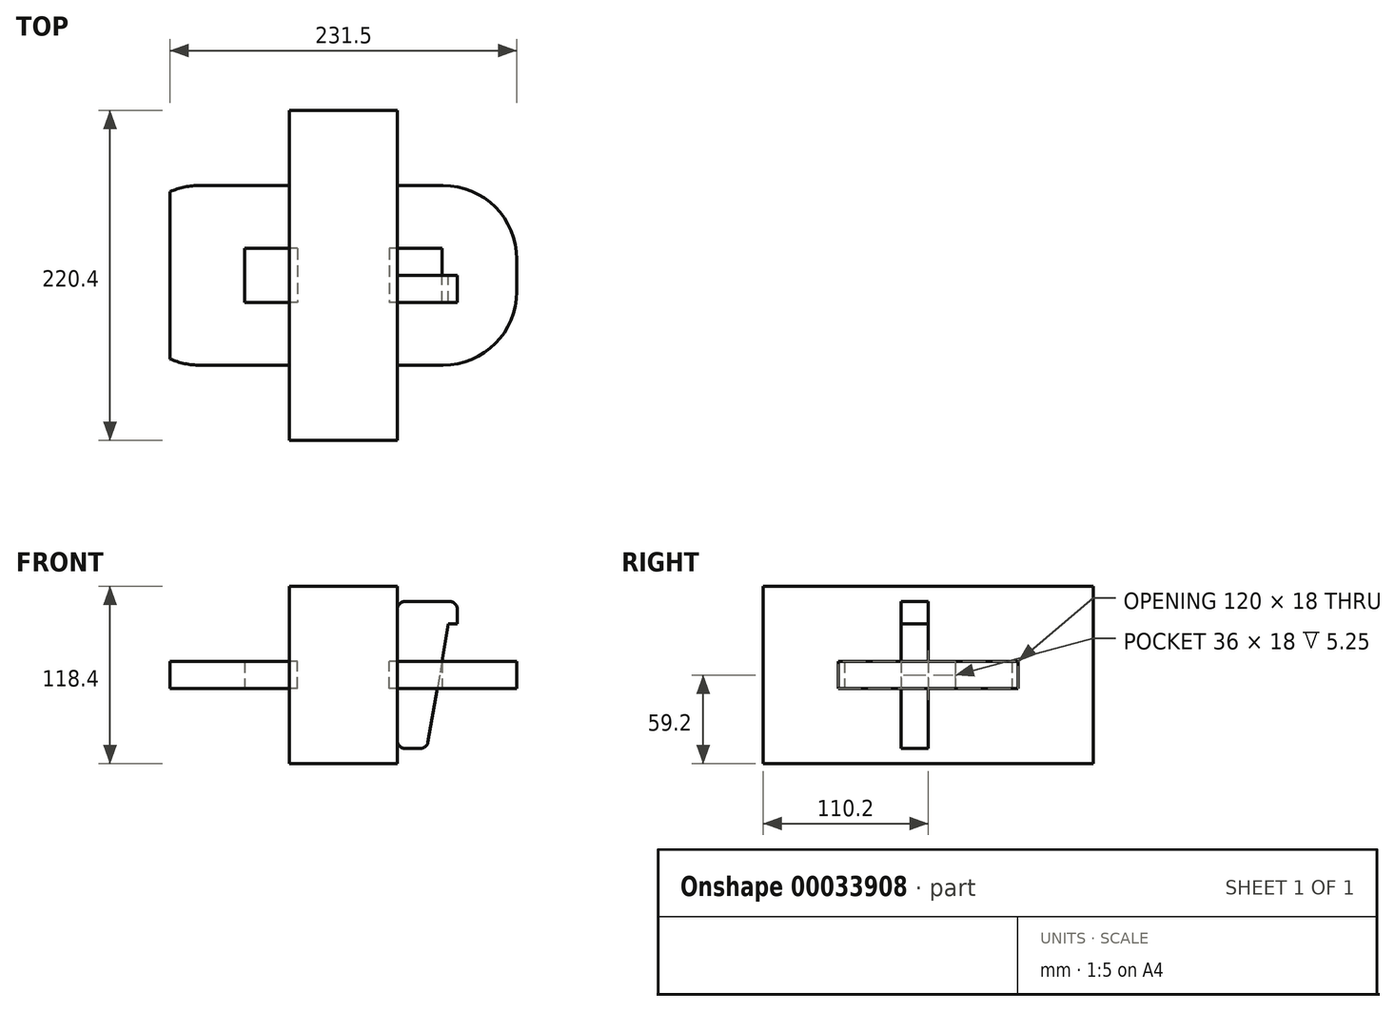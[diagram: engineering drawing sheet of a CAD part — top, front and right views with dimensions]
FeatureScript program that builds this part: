
annotation { "Feature Type Name" : "Feature", "Feature Type Description" : "" }
export const myFeature = defineFeature(function(context is Context, id is Id, definition is map)
    precondition{}
    {
        {
            var Q0;
            Q0=qCreatedBy(makeId("Top.planeOp"),FACE);
            var sketch = newSketch(context, id + "F0", { "sketchPlane" : qUnion([Q0])});
            skLineSegment(sketch, "E0.rect.bottom", {"start": v(95.75, -60) * mm, "end": v(-95.75, -60) * mm});
            skLineSegment(sketch, "E0.rect.top", {"start": v(95.75, 60) * mm, "end": v(-95.75, 60) * mm});
            skLineSegment(sketch, "E0.rect.left", {"start": v(145.75, -10) * mm, "end": v(145.75, 10) * mm});
            skLineSegment(sketch, "E0.rect.right", {"start": v(-145.75, -10) * mm, "end": v(-145.75, 10) * mm});
            skPoint(sketch, "E0.rect.middle", {"position": v(0, 0) * mm});
            skLineSegment(sketch, "E1.rect.bottom", {"start": v(65.75, -18) * mm, "end": v(-65.75, -18) * mm});
            skLineSegment(sketch, "E1.rect.top", {"start": v(65.75, 18) * mm, "end": v(-65.75, 18) * mm});
            skLineSegment(sketch, "E1.rect.left", {"start": v(65.75, -18) * mm, "end": v(65.75, 18) * mm});
            skLineSegment(sketch, "E1.rect.right", {"start": v(-65.75, -18) * mm, "end": v(-65.75, 18) * mm});
            skLineSegment(sketch, "E2", {"start": v(0, 0) * mm, "end": v(0, 60) * mm, "construction": true});
            skLineSegment(sketch, "E3", {"start": v(0, 0) * mm, "end": v(-24.77, 0) * mm, "construction": true});
            skPoint(sketch, "E4.visualSharp", {"position": v(-145.75, 60) * mm});
            skArc(sketch, "E4.filletArc", {"start": v(-95.75, 60) * mm, "mid": v(-131.1, 45.36) * mm, "end": v(-145.75, 10) * mm});
            skPoint(sketch, "E5.visualSharp", {"position": v(-145.75, -60) * mm});
            skArc(sketch, "E5.filletArc", {"start": v(-145.75, -10) * mm, "mid": v(-131.1, -45.36) * mm, "end": v(-95.75, -60) * mm});
            skPoint(sketch, "E6.visualSharp", {"position": v(145.75, 60) * mm});
            skArc(sketch, "E6.filletArc", {"start": v(145.75, 10) * mm, "mid": v(131.1, 45.36) * mm, "end": v(95.75, 60) * mm});
            skPoint(sketch, "E7.visualSharp", {"position": v(145.75, -60) * mm});
            skArc(sketch, "E7.filletArc", {"start": v(95.75, -60) * mm, "mid": v(131.1, -45.36) * mm, "end": v(145.75, -10) * mm});
            skSolve(sketch);
        }
        {
            var Q0;
            Q0 = qSketchRegion(id + "F0", true);
            var Q1;
            Q1=makeQuery(id+"F0.imprint","IMPRINT",FACE,{"disambiguationData":[TD([[makeQuery(id+"F0.imprint","IMPRINT",EDGE,{"derivedFrom":sQuery(id+"F0.wireOp",EDGE,"E0.rect.bottom")}),-1.0]])]});
            extrude(context, id + "F1", {"entities" : qUnion([Q0, Q1]), "depth" : 18 * mm});
        }
        {
            var Q0;
            Q0=qCreatedBy(makeId("Right.planeOp"),FACE);
            var sketch = newSketch(context, id + "F2", { "sketchPlane" : qUnion([Q0])});
            skLineSegment(sketch, "E8.0", {"start": v(-60, 18) * mm, "end": v(-60, 0) * mm});
            skLineSegment(sketch, "E8.1", {"start": v(-60, 18) * mm, "end": v(-10, 18) * mm});
            skLineSegment(sketch, "E8.2", {"start": v(-60, 0) * mm, "end": v(-10, 0) * mm});
            skLineSegment(sketch, "E8.3", {"start": v(-10, 18) * mm, "end": v(10, 18) * mm});
            skLineSegment(sketch, "E8.4", {"start": v(10, 18) * mm, "end": v(60, 18) * mm});
            skLineSegment(sketch, "E8.5", {"start": v(10, 0) * mm, "end": v(60, 0) * mm});
            skLineSegment(sketch, "E8.6", {"start": v(-10, 0) * mm, "end": v(10, 0) * mm});
            skLineSegment(sketch, "E8.7", {"start": v(60, 18) * mm, "end": v(60, 0) * mm});
            skLineSegment(sketch, "E9.0", {"start": v(10, 68.2) * mm, "end": v(110.2, 68.2) * mm});
            skLineSegment(sketch, "E9.1", {"start": v(-10, 68.2) * mm, "end": v(10, 68.2) * mm});
            skLineSegment(sketch, "E9.2", {"start": v(-110.2, 68.2) * mm, "end": v(-10, 68.2) * mm});
            skLineSegment(sketch, "E9.3", {"start": v(-110.2, 68.2) * mm, "end": v(-110.2, -50.2) * mm});
            skLineSegment(sketch, "E9.4", {"start": v(-110.2, -50.2) * mm, "end": v(-10, -50.2) * mm});
            skLineSegment(sketch, "E9.5", {"start": v(110.2, 68.2) * mm, "end": v(110.2, -50.2) * mm});
            skLineSegment(sketch, "E9.6", {"start": v(-10, -50.2) * mm, "end": v(10, -50.2) * mm});
            skLineSegment(sketch, "E9.7", {"start": v(10, -50.2) * mm, "end": v(110.2, -50.2) * mm});
            skSolve(sketch);
        }
        {
            var Q0;
            Q0=makeQuery(id+"F2.imprint","IMPRINT",FACE,{"disambiguationData":[TD([[makeQuery(id+"F2.imprint","IMPRINT",EDGE,{"derivedFrom":sQuery(id+"F2.wireOp",EDGE,"E8.0")}),-1.0]])]});
            extrude(context, id + "F3", {"entities" : qUnion([Q0]), "endBound" : BoundingType.SYMMETRIC, "depth" : 72 * mm});
        }
        {
            var Q0;
            Q0=makeQuery(id+"F1.opExtrude","CAP_FACE",FACE,{"disambiguationData":[OSD([sQuery(id+"F0.wireOp",EDGE,"E0.rect.bottom"),sQuery(id+"F0.wireOp",EDGE,"E0.rect.top"),sQuery(id+"F0.wireOp",EDGE,"E0.rect.left"),sQuery(id+"F0.wireOp",EDGE,"E0.rect.right"),sQuery(id+"F0.wireOp",EDGE,"E1.rect.bottom"),sQuery(id+"F0.wireOp",EDGE,"E1.rect.top"),sQuery(id+"F0.wireOp",EDGE,"E1.rect.left"),sQuery(id+"F0.wireOp",EDGE,"E1.rect.right"),sQuery(id+"F0.wireOp",EDGE,"E4.filletArc"),sQuery(id+"F0.wireOp",EDGE,"E5.filletArc"),sQuery(id+"F0.wireOp",EDGE,"E6.filletArc"),sQuery(id+"F0.wireOp",EDGE,"E7.filletArc")])],"isStart":false});
            var sketch = newSketch(context, id + "F4", { "sketchPlane" : qUnion([Q0])});
            skLineSegment(sketch, "E10", {"start": v(-65.75, -18) * mm, "end": v(-30.75, -18) * mm});
            skLineSegment(sketch, "E11", {"start": v(-30.75, -18) * mm, "end": v(-30.75, 18) * mm});
            skLineSegment(sketch, "E12", {"start": v(-30.75, 18) * mm, "end": v(0, 18) * mm});
            skLineSegment(sketch, "E13", {"start": v(0, 18) * mm, "end": v(0, -18) * mm});
            skLineSegment(sketch, "E14", {"start": v(0, -18) * mm, "end": v(-30.75, -18) * mm});
            skLineSegment(sketch, "E15.MirrorCS", {"start": v(0, -18) * mm, "end": v(30.75, -18) * mm});
            skLineSegment(sketch, "E16.MirrorCS", {"start": v(30.75, -18) * mm, "end": v(30.75, 18) * mm});
            skLineSegment(sketch, "E17.MirrorCS", {"start": v(30.75, 18) * mm, "end": v(0, 18) * mm});
            skSolve(sketch);
        }
        {
            var Q0;
            Q0 = qSketchRegion(id + "F4", true);
            extrude(context, id + "F5", {"entities" : qUnion([Q0]), "operationType" : NewBodyOperationType.ADD, "endBound" : BoundingType.UP_TO_NEXT, "oppositeDirection" : true, "depth" : 25 * mm});
        }
        {
            var Q0;
            Q0=makeQuery(id+"F5.boolean.opBoolean","MERGE",FACE,{"derivedFrom":[makeQuery(id+"F1.opExtrude","CAP_FACE",FACE,{"disambiguationData":[OSD([sQuery(id+"F0.wireOp",EDGE,"E0.rect.bottom"),sQuery(id+"F0.wireOp",EDGE,"E0.rect.top"),sQuery(id+"F0.wireOp",EDGE,"E0.rect.left"),sQuery(id+"F0.wireOp",EDGE,"E0.rect.right"),sQuery(id+"F0.wireOp",EDGE,"E1.rect.bottom"),sQuery(id+"F0.wireOp",EDGE,"E1.rect.top"),sQuery(id+"F0.wireOp",EDGE,"E1.rect.left"),sQuery(id+"F0.wireOp",EDGE,"E1.rect.right"),sQuery(id+"F0.wireOp",EDGE,"E4.filletArc"),sQuery(id+"F0.wireOp",EDGE,"E5.filletArc"),sQuery(id+"F0.wireOp",EDGE,"E6.filletArc"),sQuery(id+"F0.wireOp",EDGE,"E7.filletArc")])],"isStart":false}),makeQuery(id+"F5.opExtrude","CAP_FACE",FACE,{"disambiguationData":[OSD([sQuery(id+"F4.wireOp",EDGE,"E11"),sQuery(id+"F4.wireOp",EDGE,"E12"),sQuery(id+"F4.wireOp",EDGE,"E14"),sQuery(id+"F4.wireOp",EDGE,"E15.MirrorCS"),sQuery(id+"F4.wireOp",EDGE,"E16.MirrorCS"),sQuery(id+"F4.wireOp",EDGE,"E17.MirrorCS")])],"isStart":true})]});
            var sketch = newSketch(context, id + "F6", { "sketchPlane" : qUnion([Q0])});
            skLineSegment(sketch, "E18.rect.bottom", {"start": v(-115.75, -60) * mm, "end": v(115.75, -60) * mm});
            skLineSegment(sketch, "E18.rect.top", {"start": v(-115.75, 60) * mm, "end": v(115.75, 60) * mm});
            skLineSegment(sketch, "E18.rect.left", {"start": v(-115.75, -60) * mm, "end": v(-115.75, 60) * mm});
            skLineSegment(sketch, "E18.rect.right", {"start": v(115.75, -60) * mm, "end": v(115.75, 60) * mm});
            skPoint(sketch, "E18.rect.middle", {"position": v(0, 0) * mm});
            skLineSegment(sketch, "E19", {"start": v(-115.75, 60) * mm, "end": v(-171.14, 60) * mm});
            skLineSegment(sketch, "E20", {"start": v(-171.14, 60) * mm, "end": v(-171.14, -60) * mm});
            skLineSegment(sketch, "E21", {"start": v(-171.14, -60) * mm, "end": v(-115.75, -60) * mm});
            skLineSegment(sketch, "E22", {"start": v(115.75, -60) * mm, "end": v(180.93, -60) * mm});
            skLineSegment(sketch, "E23", {"start": v(180.93, -60) * mm, "end": v(180.93, 60) * mm});
            skLineSegment(sketch, "E24", {"start": v(180.93, 60) * mm, "end": v(115.75, 60) * mm});
            skSolve(sketch);
        }
        {
            var Q0;
            {var subQ7=sQuery(id+"F6.wireOp",EDGE,"E19");Q0=makeQuery(id+"F6.imprint","IMPRINT",FACE,{"disambiguationData":[TD([[makeQuery(id+"F6.imprint","IMPRINT",EDGE,{"derivedFrom":subQ7}),1.0]])]});}
            var Q1;
            {var subQ7=sQuery(id+"F6.wireOp",EDGE,"E22");Q1=makeQuery(id+"F6.imprint","IMPRINT",FACE,{"disambiguationData":[TD([[makeQuery(id+"F6.imprint","IMPRINT",EDGE,{"derivedFrom":subQ7}),1.0]])]});}
            var Q2;
            {var subQ3=makeQuery(id+"F1.opExtrude","CAP_EDGE",EDGE,{"disambiguationData":[OSD([sQuery(id+"F0.wireOp",EDGE,"E0.rect.right")])],"isStart":false});Q2=makeQuery(id+"F6.imprint","IMPRINT",FACE,{"disambiguationData":[TD([[makeQuery(id+"F6.imprint","IMPRINT",EDGE,{"derivedFrom":subQ3}),-1.0]])]});}
            var Q3;
            {var subQ3=makeQuery(id+"F1.opExtrude","CAP_EDGE",EDGE,{"disambiguationData":[OSD([sQuery(id+"F0.wireOp",EDGE,"E0.rect.left")])],"isStart":false});Q3=makeQuery(id+"F6.imprint","IMPRINT",FACE,{"disambiguationData":[TD([[makeQuery(id+"F6.imprint","IMPRINT",EDGE,{"derivedFrom":subQ3}),1.0]])]});}
            extrude(context, id + "F7", {"entities" : qUnion([Q0, Q1, Q2, Q3]), "operationType" : NewBodyOperationType.REMOVE, "oppositeDirection" : true, "depth" : 25 * mm});
        }
        {
            var Q0;
            {var subQ0=makeQuery(id+"F1.opExtrude","CAP_EDGE",EDGE,{"disambiguationData":[OSD([sQuery(id+"F0.wireOp",EDGE,"E4.filletArc")])],"isStart":false});var subQ3=sQuery(id+"F6.wireOp",EDGE,"E18.rect.top");var subQ4=makeQuery(id+"F6.imprint","INTERSECT",VERTEX,{"derivedFrom":[subQ0,subQ3]});Q0=makeQuery(id+"F6.imprint","IMPRINT",FACE,{"disambiguationData":[TD([[makeQuery(id+"F6.imprint","IMPRINT",EDGE,{"disambiguationData":[TD([[subQ4,-1.0]])],"derivedFrom":subQ0}),-1.0]])]});}
            var Q1;
            {var subQ0=makeQuery(id+"F1.opExtrude","CAP_EDGE",EDGE,{"disambiguationData":[OSD([sQuery(id+"F0.wireOp",EDGE,"E6.filletArc")])],"isStart":false});var subQ3=sQuery(id+"F6.wireOp",EDGE,"E18.rect.top");var subQ4=makeQuery(id+"F6.imprint","INTERSECT",VERTEX,{"derivedFrom":[subQ0,subQ3]});Q1=makeQuery(id+"F6.imprint","IMPRINT",FACE,{"disambiguationData":[TD([[makeQuery(id+"F6.imprint","IMPRINT",EDGE,{"disambiguationData":[TD([[subQ4,1.0]])],"derivedFrom":subQ0}),-1.0]])]});}
            var Q2;
            {var subQ0=makeQuery(id+"F1.opExtrude","CAP_EDGE",EDGE,{"disambiguationData":[OSD([sQuery(id+"F0.wireOp",EDGE,"E7.filletArc")])],"isStart":false});var subQ3=sQuery(id+"F6.wireOp",EDGE,"E18.rect.bottom");var subQ4=makeQuery(id+"F6.imprint","INTERSECT",VERTEX,{"derivedFrom":[subQ0,subQ3]});Q2=makeQuery(id+"F6.imprint","IMPRINT",FACE,{"disambiguationData":[TD([[makeQuery(id+"F6.imprint","IMPRINT",EDGE,{"disambiguationData":[TD([[subQ4,-1.0]])],"derivedFrom":subQ0}),-1.0]])]});}
            var Q3;
            {var subQ0=makeQuery(id+"F1.opExtrude","CAP_EDGE",EDGE,{"disambiguationData":[OSD([sQuery(id+"F0.wireOp",EDGE,"E5.filletArc")])],"isStart":false});var subQ3=sQuery(id+"F6.wireOp",EDGE,"E18.rect.bottom");var subQ4=makeQuery(id+"F6.imprint","INTERSECT",VERTEX,{"derivedFrom":[subQ0,subQ3]});Q3=makeQuery(id+"F6.imprint","IMPRINT",FACE,{"disambiguationData":[TD([[makeQuery(id+"F6.imprint","IMPRINT",EDGE,{"disambiguationData":[TD([[subQ4,1.0]])],"derivedFrom":subQ0}),-1.0]])]});}
            extrude(context, id + "F8", {"entities" : qUnion([Q0, Q1, Q2, Q3]), "operationType" : NewBodyOperationType.ADD, "oppositeDirection" : true, "depth" : 18 * mm});
        }
        {
            var Q0;
            Q0=makeQuery(id+"F8.opExtrude","SWEPT_EDGE",EDGE,{"disambiguationData":[OSD([sQuery(id+"F6.wireOp",EDGE,"E18.rect.top"),sQuery(id+"F6.wireOp",EDGE,"E18.rect.left"),sQuery(id+"F6.wireOp",EDGE,"E19")])]});
            var Q1;
            Q1=makeQuery(id+"F8.opExtrude","SWEPT_EDGE",EDGE,{"disambiguationData":[OSD([sQuery(id+"F6.wireOp",EDGE,"E18.rect.bottom"),sQuery(id+"F6.wireOp",EDGE,"E18.rect.left"),sQuery(id+"F6.wireOp",EDGE,"E21")])]});
            var Q2;
            Q2=makeQuery(id+"F8.opExtrude","SWEPT_EDGE",EDGE,{"disambiguationData":[OSD([sQuery(id+"F6.wireOp",EDGE,"E18.rect.bottom"),sQuery(id+"F6.wireOp",EDGE,"E18.rect.right"),sQuery(id+"F6.wireOp",EDGE,"E22")])]});
            var Q3;
            Q3=makeQuery(id+"F8.opExtrude","SWEPT_EDGE",EDGE,{"disambiguationData":[OSD([sQuery(id+"F6.wireOp",EDGE,"E18.rect.top"),sQuery(id+"F6.wireOp",EDGE,"E18.rect.right"),sQuery(id+"F6.wireOp",EDGE,"E24")])]});
            fillet(context, id + "F9", {"entities" : qUnion([Q0, Q1, Q2, Q3]), "radius" : 49.23 * mm, "tangentPropagation" : true, "allowEdgeOverflow" : false});
        }
        {
            var Q0;
            Q0=qCreatedBy(makeId("Front.planeOp"),FACE);
            var sketch = newSketch(context, id + "F10", { "sketchPlane" : qUnion([Q0])});
            skLineSegment(sketch, "E25.0", {"start": v(36, 68.2) * mm, "end": v(36, -50.2) * mm});
            skLineSegment(sketch, "E26.1", {"start": v(65.75, 18) * mm, "end": v(65.75, 0) * mm});
            skLineSegment(sketch, "E27.0", {"start": v(66.52, 18) * mm, "end": v(-66.52, 18) * mm, "construction": true});
            skLineSegment(sketch, "E28", {"start": v(36, 18) * mm, "end": v(36, 53) * mm});
            skLineSegment(sketch, "E29.0", {"start": v(66.52, 0) * mm, "end": v(-66.52, 0) * mm, "construction": true});
            skLineSegment(sketch, "E30", {"start": v(36, 18) * mm, "end": v(36, 0) * mm});
            skLineSegment(sketch, "E31", {"start": v(36, 0) * mm, "end": v(36, -40) * mm});
            skLineSegment(sketch, "E32", {"start": v(41, 58) * mm, "end": v(71, 58) * mm});
            skLineSegment(sketch, "E33", {"start": v(65.75, 0) * mm, "end": v(65.75, -41.28) * mm, "construction": true});
            skLineSegment(sketch, "E34", {"start": v(41, -40) * mm, "end": v(51.54, -40) * mm});
            skLineSegment(sketch, "E35", {"start": v(36, -35) * mm, "end": v(36, -30) * mm});
            skLineSegment(sketch, "E36", {"start": v(36, 18) * mm, "end": v(65.75, 18) * mm});
            skLineSegment(sketch, "E37", {"start": v(65.75, 18) * mm, "end": v(56.47, -35.85) * mm});
            skLineSegment(sketch, "E38", {"start": v(65.75, 18) * mm, "end": v(70.06, 43) * mm});
            skLineSegment(sketch, "E39", {"start": v(36, 18) * mm, "end": v(36, 43) * mm});
            skLineSegment(sketch, "E40", {"start": v(36, 43) * mm, "end": v(98.36, 43) * mm, "construction": true});
            skLineSegment(sketch, "E41", {"start": v(70.06, 43) * mm, "end": v(76, 43) * mm});
            skLineSegment(sketch, "E42", {"start": v(76, 43) * mm, "end": v(76, 53) * mm});
            skPoint(sketch, "E43.visualSharp", {"position": v(76, 58) * mm});
            skArc(sketch, "E43.filletArc", {"start": v(76, 53) * mm, "mid": v(74.54, 56.54) * mm, "end": v(71, 58) * mm});
            skPoint(sketch, "E44.visualSharp", {"position": v(36, 58) * mm});
            skArc(sketch, "E44.filletArc", {"start": v(41, 58) * mm, "mid": v(37.46, 56.54) * mm, "end": v(36, 53) * mm});
            skPoint(sketch, "E45.visualSharp", {"position": v(36, -40) * mm});
            skArc(sketch, "E45.filletArc", {"start": v(36, -35) * mm, "mid": v(37.46, -38.54) * mm, "end": v(41, -40) * mm});
            skPoint(sketch, "E46.visualSharp", {"position": v(55.75, -40) * mm});
            skArc(sketch, "E46.filletArc", {"start": v(51.54, -40) * mm, "mid": v(54.76, -38.82) * mm, "end": v(56.47, -35.85) * mm});
            skSolve(sketch);
        }
        {
            var Q0;
            Q0 = qSketchRegion(id + "F10", true);
            extrude(context, id + "F11", {"entities" : qUnion([Q0]), "depth" : 18 * mm});
        }
    });
